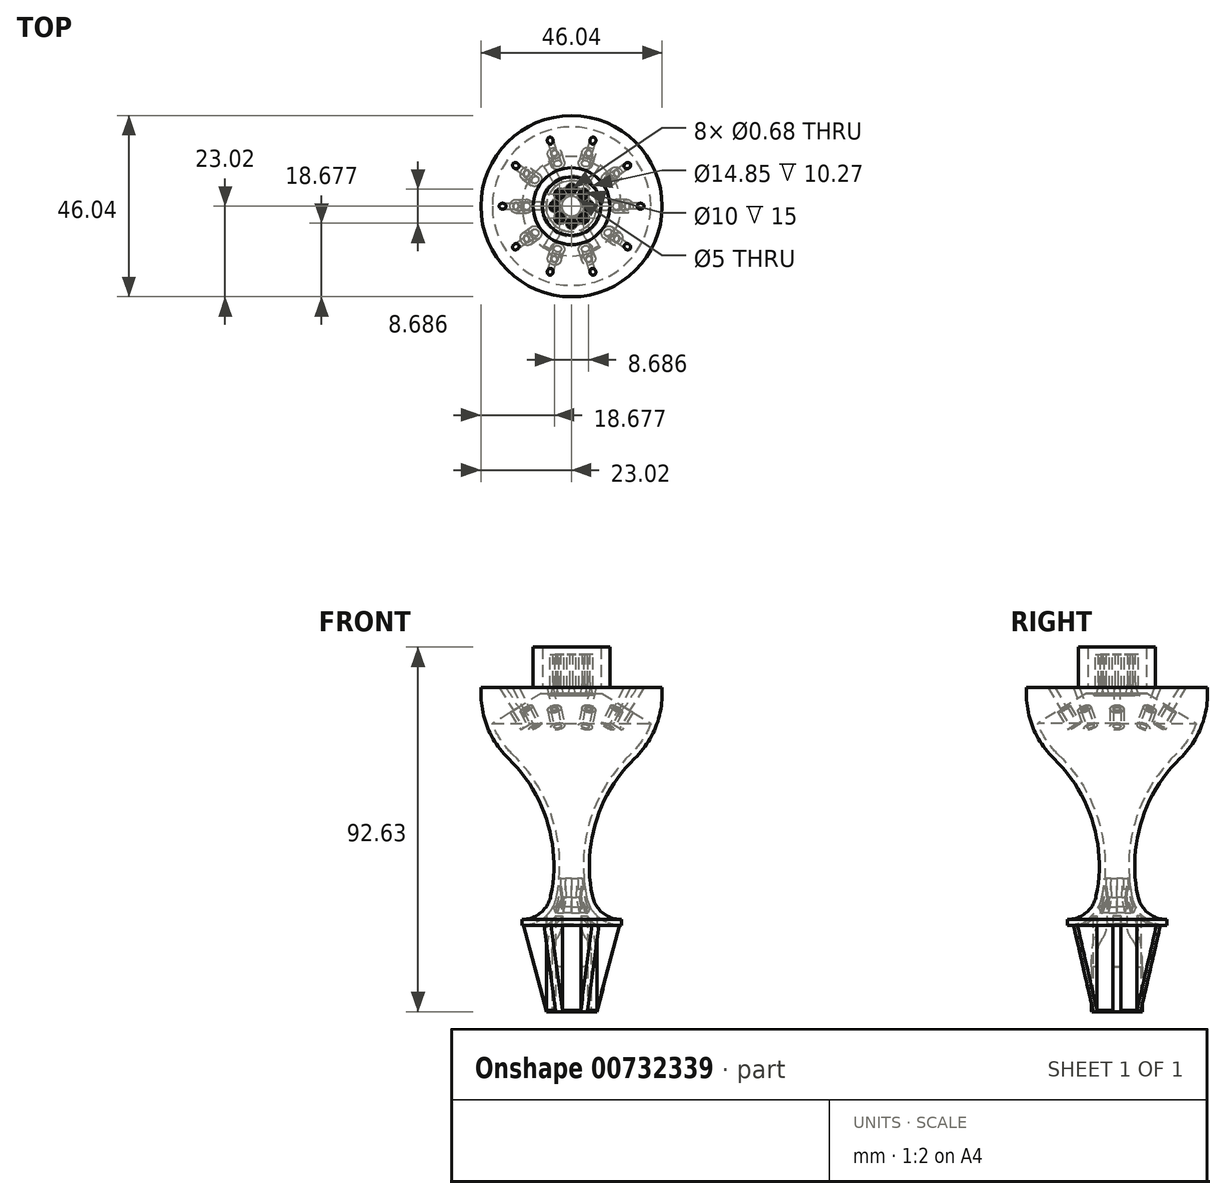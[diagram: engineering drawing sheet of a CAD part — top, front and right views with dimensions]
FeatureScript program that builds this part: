
annotation { "Feature Type Name" : "Feature", "Feature Type Description" : "" }
export const myFeature = defineFeature(function(context is Context, id is Id, definition is map)
    precondition{}
    {
        {
            var Q0;
            Q0=qCreatedBy(makeId("Front.planeOp"),FACE);
            var sketch = newSketch(context, id + "F0", { "sketchPlane" : qUnion([Q0])});
            skArc(sketch, "E0", {"start": v(16.02, 27.2) * mm, "mid": v(6.17, 11.12) * mm, "end": v(5.3, -7.72) * mm});
            skArc(sketch, "E1", {"start": v(5, -22.1) * mm, "mid": v(4.71, -20.36) * mm, "end": v(3.88, -18.8) * mm});
            skLineSegment(sketch, "E2", {"start": v(5, -22.1) * mm, "end": v(5, -37.1) * mm});
            skLineSegment(sketch, "E3", {"start": v(6.5, -25.66) * mm, "end": v(6.5, -37.1) * mm});
            skArc(sketch, "E4.trimOffspring", {"start": v(2.5, -14.83) * mm, "mid": v(2.87, -16.93) * mm, "end": v(3.88, -18.8) * mm});
            skLineSegment(sketch, "E5", {"start": v(6.5, -37.1) * mm, "end": v(5, -37.1) * mm});
            skArc(sketch, "E6.trimOffspring", {"start": v(29.62, -0.11) * mm, "mid": v(29.62, -0.06) * mm, "end": v(29.62, 0) * mm});
            skArc(sketch, "E7", {"start": v(6.5, -25.66) * mm, "mid": v(5.49, -16.67) * mm, "end": v(2.5, -8.12) * mm});
            skPoint(sketch, "E8.start.orphan", {"position": v(3, -9.22) * mm});
            skLineSegment(sketch, "E9", {"start": v(2.5, -14.83) * mm, "end": v(2.5, -8.12) * mm});
            skArc(sketch, "E10", {"start": v(14.97, 28.28) * mm, "mid": v(4.73, 11.56) * mm, "end": v(3.83, -8.02) * mm});
            skLineSegment(sketch, "E11", {"start": v(0, 43.76) * mm, "end": v(21.52, 43.76) * mm});
            skLineSegment(sketch, "E12", {"start": v(0, 43.76) * mm, "end": v(0, 45.26) * mm});
            skLineSegment(sketch, "E13", {"start": v(0, 45.26) * mm, "end": v(7.43, 45.26) * mm});
            skLineSegment(sketch, "E14", {"start": v(23.02, 45.26) * mm, "end": v(23.02, 43.76) * mm});
            skPoint(sketch, "E15", {"position": v(0, 0) * mm});
            skArc(sketch, "E16", {"start": v(14.97, 28.28) * mm, "mid": v(19.82, 35.35) * mm, "end": v(21.52, 43.76) * mm});
            skArc(sketch, "E17", {"start": v(16.02, 27.2) * mm, "mid": v(21.2, 34.77) * mm, "end": v(23.02, 43.76) * mm});
            skArc(sketch, "E18", {"start": v(3.83, -8.02) * mm, "mid": v(6.96, -13.17) * mm, "end": v(12.64, -15.19) * mm});
            skArc(sketch, "E19", {"start": v(5.3, -7.72) * mm, "mid": v(7.9, -12) * mm, "end": v(12.64, -13.69) * mm});
            skLineSegment(sketch, "E20", {"start": v(12.64, -13.69) * mm, "end": v(12.64, -15.19) * mm});
            skLineSegment(sketch, "E21.top", {"start": v(7.43, 55.53) * mm, "end": v(9.75, 55.53) * mm});
            skLineSegment(sketch, "E21.left", {"start": v(7.43, 45.26) * mm, "end": v(7.43, 55.53) * mm});
            skLineSegment(sketch, "E21.right", {"start": v(9.75, 45.26) * mm, "end": v(9.75, 55.53) * mm});
            skLineSegment(sketch, "E22.trimOffspring", {"start": v(9.75, 45.26) * mm, "end": v(23.02, 45.26) * mm});
            skPoint(sketch, "E23", {"position": v(3, 0) * mm});
            skSolve(sketch);
        }
        {
            var Q0;
            Q0 = qSketchRegion(id + "F0", true);
            var Q1;
            Q1=sQuery(id+"F0.wireOp",EDGE,"E12");
            revolve(context, id + "F1", {"surfaceOperationType" : NewSurfaceOperationType.NEW, "entities" : qUnion([Q0]), "axis" : qUnion([Q1]), "revolveType" : RevolveType.FULL});
        }
        {
            var Q0;
            Q0=qCreatedBy(makeId("Front.planeOp"),FACE);
            var sketch = newSketch(context, id + "F2", { "sketchPlane" : qUnion([Q0])});
            skLineSegment(sketch, "E24.bottom", {"start": v(4.34, 45.26) * mm, "end": v(4.85, 45.26) * mm});
            skLineSegment(sketch, "E24.top", {"start": v(4.34, 43.76) * mm, "end": v(5.25, 43.76) * mm});
            skLineSegment(sketch, "E24.left", {"start": v(4.34, 45.26) * mm, "end": v(4.34, 43.76) * mm});
            skLineSegment(sketch, "E25", {"start": v(4.85, 45.26) * mm, "end": v(5.25, 43.76) * mm});
            skSolve(sketch);
        }
        {
            var Q0;
            Q0=makeQuery(id+"F2.imprint","IMPRINT",FACE,{"disambiguationData":[TD([[makeQuery(id+"F2.imprint","IMPRINT",EDGE,{"derivedFrom":sQuery(id+"F2.wireOp",EDGE,"E24.bottom")}),-1.0]])]});
            var Q1;
            Q1=sQuery(id+"F2.wireOp",EDGE,"E24.left");
            revolve(context, id + "F3", {"surfaceOperationType" : NewSurfaceOperationType.NEW, "entities" : qUnion([Q0]), "axis" : qUnion([Q1]), "revolveType" : RevolveType.FULL});
        }
        {
            var Q0;
            Q0=makeQuery(id+"F3.opRevolve","SWEPT_BODY",BODY,{"disambiguationData":[OSD([sQuery(id+"F2.wireOp",EDGE,"E24.bottom"),sQuery(id+"F2.wireOp",EDGE,"E24.top"),sQuery(id+"F2.wireOp",EDGE,"E24.left"),sQuery(id+"F2.wireOp",EDGE,"E24.right")])]});
            var Q1;
            Q1=makeQuery(id+"F1.opRevolve","SWEPT_FACE",FACE,{"disambiguationData":[OSD([sQuery(id+"F0.wireOp",EDGE,"E14")])]});
            circularPattern(context, id + "F4", {"entities" : qUnion([Q0]), "axis" : qUnion([Q1]), "angle" : 360 * degree, "instanceCount" : 8, "equalSpace" : true});
        }
        {
            var Q0;
            Q0=makeQuery(id+"F3.opRevolve","SWEPT_BODY",BODY,{"disambiguationData":[OSD([sQuery(id+"F2.wireOp",EDGE,"E24.bottom"),sQuery(id+"F2.wireOp",EDGE,"E24.top"),sQuery(id+"F2.wireOp",EDGE,"E24.left"),sQuery(id+"F2.wireOp",EDGE,"E24.right")])]});
            var Q1;
            Q1=makeQuery(id+"F4.opPattern","COPY",BODY,{"derivedFrom":makeQuery(id+"F3.opRevolve","SWEPT_BODY",BODY,{"disambiguationData":[OSD([sQuery(id+"F2.wireOp",EDGE,"E24.bottom"),sQuery(id+"F2.wireOp",EDGE,"E24.top"),sQuery(id+"F2.wireOp",EDGE,"E24.left"),sQuery(id+"F2.wireOp",EDGE,"E24.right")])]}),"instanceName":"7"});
            var Q2;
            Q2=makeQuery(id+"F4.opPattern","COPY",BODY,{"derivedFrom":makeQuery(id+"F3.opRevolve","SWEPT_BODY",BODY,{"disambiguationData":[OSD([sQuery(id+"F2.wireOp",EDGE,"E24.bottom"),sQuery(id+"F2.wireOp",EDGE,"E24.top"),sQuery(id+"F2.wireOp",EDGE,"E24.left"),sQuery(id+"F2.wireOp",EDGE,"E24.right")])]}),"instanceName":"6"});
            var Q3;
            Q3=makeQuery(id+"F4.opPattern","COPY",BODY,{"derivedFrom":makeQuery(id+"F3.opRevolve","SWEPT_BODY",BODY,{"disambiguationData":[OSD([sQuery(id+"F2.wireOp",EDGE,"E24.bottom"),sQuery(id+"F2.wireOp",EDGE,"E24.top"),sQuery(id+"F2.wireOp",EDGE,"E24.left"),sQuery(id+"F2.wireOp",EDGE,"E24.right")])]}),"instanceName":"5"});
            var Q4;
            Q4=makeQuery(id+"F4.opPattern","COPY",BODY,{"derivedFrom":makeQuery(id+"F3.opRevolve","SWEPT_BODY",BODY,{"disambiguationData":[OSD([sQuery(id+"F2.wireOp",EDGE,"E24.bottom"),sQuery(id+"F2.wireOp",EDGE,"E24.top"),sQuery(id+"F2.wireOp",EDGE,"E24.left"),sQuery(id+"F2.wireOp",EDGE,"E24.right")])]}),"instanceName":"4"});
            var Q5;
            Q5=makeQuery(id+"F4.opPattern","COPY",BODY,{"derivedFrom":makeQuery(id+"F3.opRevolve","SWEPT_BODY",BODY,{"disambiguationData":[OSD([sQuery(id+"F2.wireOp",EDGE,"E24.bottom"),sQuery(id+"F2.wireOp",EDGE,"E24.top"),sQuery(id+"F2.wireOp",EDGE,"E24.left"),sQuery(id+"F2.wireOp",EDGE,"E24.right")])]}),"instanceName":"3"});
            var Q6;
            Q6=makeQuery(id+"F4.opPattern","COPY",BODY,{"derivedFrom":makeQuery(id+"F3.opRevolve","SWEPT_BODY",BODY,{"disambiguationData":[OSD([sQuery(id+"F2.wireOp",EDGE,"E24.bottom"),sQuery(id+"F2.wireOp",EDGE,"E24.top"),sQuery(id+"F2.wireOp",EDGE,"E24.left"),sQuery(id+"F2.wireOp",EDGE,"E24.right")])]}),"instanceName":"2"});
            var Q7;
            Q7=makeQuery(id+"F4.opPattern","COPY",BODY,{"derivedFrom":makeQuery(id+"F3.opRevolve","SWEPT_BODY",BODY,{"disambiguationData":[OSD([sQuery(id+"F2.wireOp",EDGE,"E24.bottom"),sQuery(id+"F2.wireOp",EDGE,"E24.top"),sQuery(id+"F2.wireOp",EDGE,"E24.left"),sQuery(id+"F2.wireOp",EDGE,"E24.right")])]}),"instanceName":"1"});
            var Q8;
            Q8=makeQuery(id+"F1.opRevolve","SWEPT_BODY",BODY,{"disambiguationData":[OSD([sQuery(id+"F0.wireOp",EDGE,"E0"),sQuery(id+"F0.wireOp",EDGE,"E10"),sQuery(id+"F0.wireOp",EDGE,"E11"),sQuery(id+"F0.wireOp",EDGE,"E12"),sQuery(id+"F0.wireOp",EDGE,"E13"),sQuery(id+"F0.wireOp",EDGE,"E14"),sQuery(id+"F0.wireOp",EDGE,"E16"),sQuery(id+"F0.wireOp",EDGE,"E17"),sQuery(id+"F0.wireOp",EDGE,"E18"),sQuery(id+"F0.wireOp",EDGE,"E19"),sQuery(id+"F0.wireOp",EDGE,"E20"),sQuery(id+"F0.wireOp",EDGE,"E21.top"),sQuery(id+"F0.wireOp",EDGE,"E21.left"),sQuery(id+"F0.wireOp",EDGE,"E21.right"),sQuery(id+"F0.wireOp",EDGE,"E22.trimOffspring")])]});
            booleanBodies(context, id + "F5", {"operationType" : BooleanOperationType.SUBTRACTION, "tools" : qUnion([Q0, Q1, Q2, Q3, Q4, Q5, Q6, Q7]), "targets" : qUnion([Q8])});
        }
        {
            var Q0;
            Q0=qCreatedBy(makeId("Top.planeOp"),FACE);
            var sketch = newSketch(context, id + "F6", { "sketchPlane" : qUnion([Q0])});
            skLineSegment(sketch, "E26.bottom", {"start": v(-74.62, 0) * mm, "end": v(74.62, 0) * mm});
            skLineSegment(sketch, "E26.top", {"start": v(-74.62, -35.92) * mm, "end": v(74.62, -35.92) * mm});
            skLineSegment(sketch, "E26.left", {"start": v(-74.62, 0) * mm, "end": v(-74.62, -35.92) * mm});
            skLineSegment(sketch, "E26.right", {"start": v(74.62, 0) * mm, "end": v(74.62, -35.92) * mm});
            skSolve(sketch);
        }
        {
            var Q0;
            Q0=qCreatedBy(makeId("Front.planeOp"),FACE);
            var sketch = newSketch(context, id + "F7", { "sketchPlane" : qUnion([Q0])});
            skLineSegment(sketch, "E27", {"start": v(17.45, 43.4) * mm, "end": v(12.2, 34.89) * mm});
            skLineSegment(sketch, "E28", {"start": v(12.2, 34.89) * mm, "end": v(12.87, 34.47) * mm});
            skLineSegment(sketch, "E29", {"start": v(12.87, 34.47) * mm, "end": v(18.13, 42.97) * mm});
            skLineSegment(sketch, "E30", {"start": v(18.13, 42.97) * mm, "end": v(17.45, 43.4) * mm});
            skSolve(sketch);
        }
        {
            var Q0;
            Q0=qCreatedBy(makeId("Front.planeOp"),FACE);
            var sketch = newSketch(context, id + "F8", { "sketchPlane" : qUnion([Q0])});
            skLineSegment(sketch, "E31", {"start": v(7.75, 43.76) * mm, "end": v(21.84, 43.76) * mm});
            skLineSegment(sketch, "E32", {"start": v(21.84, 43.76) * mm, "end": v(21.36, 35.38) * mm});
            skLineSegment(sketch, "E33", {"start": v(21.36, 35.38) * mm, "end": v(7.75, 43.76) * mm});
            skSolve(sketch);
        }
        {
            var Q0;
            Q0=qCreatedBy(makeId("Front.planeOp"),FACE);
            var sketch = newSketch(context, id + "F9", { "sketchPlane" : qUnion([Q0])});
            skLineSegment(sketch, "E34", {"start": v(20.58, 48.74) * mm, "end": v(14.45, 38.9) * mm});
            skLineSegment(sketch, "E35", {"start": v(14.45, 38.9) * mm, "end": v(13.8, 39.29) * mm});
            skLineSegment(sketch, "E36", {"start": v(13.8, 39.29) * mm, "end": v(19.94, 49.14) * mm});
            skLineSegment(sketch, "E37", {"start": v(20.58, 48.74) * mm, "end": v(19.94, 49.14) * mm});
            skSolve(sketch);
        }
        {
            var Q0;
            Q0=makeQuery(id+"F8.imprint","IMPRINT",FACE,{"disambiguationData":[TD([[makeQuery(id+"F8.imprint","IMPRINT",EDGE,{"derivedFrom":sQuery(id+"F8.wireOp",EDGE,"E31")}),-1.0]])]});
            var Q1;
            Q1=makeQuery(id+"F1.opRevolve","SWEPT_FACE",FACE,{"disambiguationData":[OSD([sQuery(id+"F0.wireOp",EDGE,"E14")])]});
            revolve(context, id + "F10", {"operationType" : NewBodyOperationType.ADD, "surfaceOperationType" : NewSurfaceOperationType.NEW, "entities" : qUnion([Q0]), "axis" : qUnion([Q1]), "revolveType" : RevolveType.FULL});
        }
        {
            var Q0;
            Q0=makeQuery(id+"F9.imprint","IMPRINT",FACE,{"disambiguationData":[TD([[makeQuery(id+"F9.imprint","IMPRINT",EDGE,{"derivedFrom":sQuery(id+"F9.wireOp",EDGE,"E34")}),-1.0]])]});
            var Q1;
            Q1=sQuery(id+"F9.wireOp",EDGE,"E36");
            revolve(context, id + "F11", {"surfaceOperationType" : NewSurfaceOperationType.NEW, "entities" : qUnion([Q0]), "axis" : qUnion([Q1]), "revolveType" : RevolveType.FULL});
        }
        {
            var Q0;
            Q0=makeQuery(id+"F11.opRevolve","SWEPT_BODY",BODY,{"disambiguationData":[OSD([sQuery(id+"F9.wireOp",EDGE,"E34"),sQuery(id+"F9.wireOp",EDGE,"E35"),sQuery(id+"F9.wireOp",EDGE,"E36"),sQuery(id+"F9.wireOp",EDGE,"E37")])]});
            var Q1;
            Q1=makeQuery(id+"F1.opRevolve","SWEPT_FACE",FACE,{"disambiguationData":[OSD([sQuery(id+"F0.wireOp",EDGE,"E14")])]});
            circularPattern(context, id + "F12", {"operationType" : NewBodyOperationType.REMOVE, "entities" : qUnion([Q0]), "axis" : qUnion([Q1]), "angle" : 360 * degree, "instanceCount" : 10, "equalSpace" : true});
        }
        {
            var Q0;
            Q0=makeQuery(id+"F7.imprint","IMPRINT",FACE,{"disambiguationData":[TD([[makeQuery(id+"F7.imprint","IMPRINT",EDGE,{"derivedFrom":sQuery(id+"F7.wireOp",EDGE,"E27")}),1.0]])]});
            var Q1;
            Q1=makeQuery(id+"F12.boolean.opBoolean","COPY",FACE,{"derivedFrom":makeQuery(id+"F11.opRevolve","SWEPT_FACE",FACE,{"disambiguationData":[OSD([sQuery(id+"F9.wireOp",EDGE,"E34")])]})});
            revolve(context, id + "F13", {"surfaceOperationType" : NewSurfaceOperationType.NEW, "entities" : qUnion([Q0]), "axis" : qUnion([Q1]), "revolveType" : RevolveType.FULL});
        }
        {
            var Q0;
            Q0=makeQuery(id+"F13.opRevolve","SWEPT_BODY",BODY,{"disambiguationData":[OSD([sQuery(id+"F7.wireOp",EDGE,"E27"),sQuery(id+"F7.wireOp",EDGE,"E28"),sQuery(id+"F7.wireOp",EDGE,"E29"),sQuery(id+"F7.wireOp",EDGE,"E30")])]});
            var Q1;
            Q1=makeQuery(id+"F1.opRevolve","SWEPT_FACE",FACE,{"disambiguationData":[OSD([sQuery(id+"F0.wireOp",EDGE,"E14")])]});
            circularPattern(context, id + "F14", {"operationType" : NewBodyOperationType.ADD, "entities" : qUnion([Q0]), "axis" : qUnion([Q1]), "angle" : 360 * degree, "instanceCount" : 10, "equalSpace" : true});
        }
        {
            var Q0;
            Q0=qCreatedBy(makeId("Front.planeOp"),FACE);
            var sketch = newSketch(context, id + "F15", { "sketchPlane" : qUnion([Q0])});
            skArc(sketch, "E38", {"start": v(5.27, 43.77) * mm, "mid": v(5.5, 43.44) * mm, "end": v(5.82, 43.2) * mm});
            skLineSegment(sketch, "E39", {"start": v(5.82, 43.77) * mm, "end": v(5.82, 43.2) * mm});
            skLineSegment(sketch, "E40", {"start": v(5.82, 43.77) * mm, "end": v(5.27, 43.77) * mm});
            skSolve(sketch);
        }
        {
            var Q0;
            Q0=makeQuery(id+"F15.imprint","IMPRINT",FACE,{"disambiguationData":[TD([[makeQuery(id+"F15.imprint","IMPRINT",EDGE,{"derivedFrom":sQuery(id+"F15.wireOp",EDGE,"E38")}),1.0]])]});
            var Q1;
            Q1=sQuery(id+"F2.wireOp",EDGE,"E24.left");
            revolve(context, id + "F16", {"surfaceOperationType" : NewSurfaceOperationType.NEW, "entities" : qUnion([Q0]), "axis" : qUnion([Q1]), "revolveType" : RevolveType.FULL});
        }
        {
            var Q0;
            Q0=makeQuery(id+"F16.opRevolve","SWEPT_BODY",BODY,{"disambiguationData":[OSD([sQuery(id+"F15.wireOp",EDGE,"E38"),sQuery(id+"F15.wireOp",EDGE,"E39"),sQuery(id+"F15.wireOp",EDGE,"E40")])]});
            var Q1;
            Q1=makeQuery(id+"F1.opRevolve","SWEPT_FACE",FACE,{"disambiguationData":[OSD([sQuery(id+"F0.wireOp",EDGE,"E14")])]});
            circularPattern(context, id + "F17", {"operationType" : NewBodyOperationType.ADD, "entities" : qUnion([Q0]), "axis" : qUnion([Q1]), "angle" : 360 * degree, "instanceCount" : 8, "equalSpace" : true});
        }
        {
            var Q0;
            Q0=qCreatedBy(makeId("Front.planeOp"),FACE);
            var sketch = newSketch(context, id + "F18", { "sketchPlane" : qUnion([Q0])});
            skArc(sketch, "E41", {"start": v(4.68, 46.5) * mm, "mid": v(4.73, 45.87) * mm, "end": v(4.85, 45.26) * mm});
            skLineSegment(sketch, "E42", {"start": v(5.48, 46.5) * mm, "end": v(5.48, 45.26) * mm});
            skLineSegment(sketch, "E43", {"start": v(5.48, 45.26) * mm, "end": v(4.85, 45.26) * mm});
            skLineSegment(sketch, "E44.top", {"start": v(4.68, 53.6) * mm, "end": v(5.48, 53.6) * mm});
            skLineSegment(sketch, "E44.left", {"start": v(4.68, 46.5) * mm, "end": v(4.68, 53.6) * mm});
            skLineSegment(sketch, "E44.right", {"start": v(5.48, 46.5) * mm, "end": v(5.48, 53.6) * mm});
            skSolve(sketch);
        }
        {
            var Q0;
            Q0=makeQuery(id+"F18.imprint","IMPRINT",FACE,{"disambiguationData":[TD([[makeQuery(id+"F18.imprint","IMPRINT",EDGE,{"derivedFrom":sQuery(id+"F18.wireOp",EDGE,"E41")}),1.0]])]});
            var Q1;
            Q1=sQuery(id+"F2.wireOp",EDGE,"E24.left");
            revolve(context, id + "F19", {"surfaceOperationType" : NewSurfaceOperationType.NEW, "entities" : qUnion([Q0]), "axis" : qUnion([Q1]), "revolveType" : RevolveType.FULL});
        }
        {
            var Q0;
            Q0=makeQuery(id+"F19.opRevolve","SWEPT_BODY",BODY,{"disambiguationData":[OSD([sQuery(id+"F18.wireOp",EDGE,"E41"),sQuery(id+"F18.wireOp",EDGE,"qMOBOxUs-DtZF-wELl-8FNL-C7Aba4HxzTed"),sQuery(id+"F18.wireOp",EDGE,"E42"),sQuery(id+"F18.wireOp",EDGE,"E43")])]});
            var Q1;
            Q1=makeQuery(id+"F1.opRevolve","SWEPT_FACE",FACE,{"disambiguationData":[OSD([sQuery(id+"F0.wireOp",EDGE,"E14")])]});
            circularPattern(context, id + "F20", {"entities" : qUnion([Q0]), "axis" : qUnion([Q1]), "angle" : 360 * degree, "instanceCount" : 4, "equalSpace" : true});
        }
        {
            var Q0;
            Q0=makeQuery(id+"F19.opRevolve","SWEPT_BODY",BODY,{"disambiguationData":[OSD([sQuery(id+"F18.wireOp",EDGE,"E41"),sQuery(id+"F18.wireOp",EDGE,"qMOBOxUs-DtZF-wELl-8FNL-C7Aba4HxzTed"),sQuery(id+"F18.wireOp",EDGE,"E42"),sQuery(id+"F18.wireOp",EDGE,"E43")])]});
            var Q1;
            Q1=makeQuery(id+"F1.opRevolve","SWEPT_FACE",FACE,{"disambiguationData":[OSD([sQuery(id+"F0.wireOp",EDGE,"E14")])]});
            circularPattern(context, id + "F21", {"operationType" : NewBodyOperationType.ADD, "entities" : qUnion([Q0]), "axis" : qUnion([Q1]), "angle" : 360 * degree, "instanceCount" : 8, "equalSpace" : true});
        }
        {
            var Q0;
            Q0=makeQuery(id+"F1.opRevolve","SWEPT_FACE",FACE,{"disambiguationData":[OSD([sQuery(id+"F0.wireOp",EDGE,"E5")])]});
            var sketch = newSketch(context, id + "F22", { "sketchPlane" : qUnion([Q0])});
            skArc(sketch, "E45", {"start": v(6.42, -1) * mm, "mid": v(6.5, 0) * mm, "end": v(6.42, 1) * mm});
            skLineSegment(sketch, "E46", {"start": v(6.42, 1) * mm, "end": v(12.2, 1) * mm});
            skLineSegment(sketch, "E47", {"start": v(12.2, 1) * mm, "end": v(12.2, 0) * mm});
            skLineSegment(sketch, "E48.MirrorCS", {"start": v(12.2, -1) * mm, "end": v(12.2, 0) * mm});
            skLineSegment(sketch, "E49", {"start": v(12.2, -1) * mm, "end": v(6.42, -1) * mm});
            skPoint(sketch, "E50.start.orphan", {"position": v(10.97, 0) * mm});
            skSolve(sketch);
        }
        {
            var Q0;
            Q0=makeQuery(id+"F22.imprint","IMPRINT",FACE,{"disambiguationData":[TD([[makeQuery(id+"F22.imprint","IMPRINT",EDGE,{"derivedFrom":sQuery(id+"F22.wireOp",EDGE,"E45")}),-1.0]])]});
            extrude(context, id + "F23", {"entities" : qUnion([Q0]), "endBound" : BoundingType.UP_TO_NEXT, "oppositeDirection" : true, "depth" : 25 * mm, "offsetDistance" : 25 * mm});
        }
        {
            var Q0;
            Q0=makeQuery(id+"F23.opExtrude","SWEPT_BODY",BODY,{"disambiguationData":[OSD([sQuery(id+"F22.wireOp",EDGE,"E45"),sQuery(id+"F22.wireOp",EDGE,"E46"),sQuery(id+"F22.wireOp",EDGE,"E47"),sQuery(id+"F22.wireOp",EDGE,"E48.MirrorCS"),sQuery(id+"F22.wireOp",EDGE,"E49")])]});
            var Q1;
            Q1=makeQuery(id+"F1.opRevolve","SWEPT_FACE",FACE,{"disambiguationData":[OSD([sQuery(id+"F0.wireOp",EDGE,"E2")])]});
            circularPattern(context, id + "F24", {"operationType" : NewBodyOperationType.ADD, "entities" : qUnion([Q0]), "axis" : qUnion([Q1]), "angle" : 360 * degree, "instanceCount" : 6, "equalSpace" : true});
        }
        {
            var Q0;
            Q0=qCreatedBy(makeId("Front.planeOp"),FACE);
            var sketch = newSketch(context, id + "F25", { "sketchPlane" : qUnion([Q0])});
            skLineSegment(sketch, "E51", {"start": v(6.42, -37.1) * mm, "end": v(12.2, -15.19) * mm});
            skLineSegment(sketch, "E52", {"start": v(12.2, -15.19) * mm, "end": v(15.57, -15.19) * mm});
            skLineSegment(sketch, "E53", {"start": v(15.57, -15.19) * mm, "end": v(15.57, -37.1) * mm});
            skLineSegment(sketch, "E54", {"start": v(6.42, -37.1) * mm, "end": v(15.57, -37.1) * mm});
            skSolve(sketch);
        }
        {
            var Q0;
            Q0=makeQuery(id+"F25.imprint","IMPRINT",FACE,{"disambiguationData":[TD([[makeQuery(id+"F25.imprint","IMPRINT",EDGE,{"derivedFrom":sQuery(id+"F25.wireOp",EDGE,"E51")}),-1.0]])]});
            var Q1;
            Q1=makeQuery(id+"F1.opRevolve","SWEPT_FACE",FACE,{"disambiguationData":[OSD([sQuery(id+"F0.wireOp",EDGE,"E2")])]});
            revolve(context, id + "F26", {"operationType" : NewBodyOperationType.REMOVE, "surfaceOperationType" : NewSurfaceOperationType.NEW, "entities" : qUnion([Q0]), "axis" : qUnion([Q1]), "revolveType" : RevolveType.FULL, "oppositeDirection" : true});
        }
        {
            var Q0;
            Q0=qCreatedBy(makeId("Front.planeOp"),FACE);
            var sketch = newSketch(context, id + "F27", { "sketchPlane" : qUnion([Q0])});
            skLineSegment(sketch, "E55", {"start": v(2.5, -8.12) * mm, "end": v(3.13, -3.2) * mm});
            skLineSegment(sketch, "E56", {"start": v(3.13, -3.2) * mm, "end": v(4.75, -10.52) * mm});
            skLineSegment(sketch, "E57", {"start": v(4.75, -10.52) * mm, "end": v(4.12, -12) * mm});
            skLineSegment(sketch, "E58", {"start": v(4.12, -12) * mm, "end": v(2.5, -12) * mm});
            skLineSegment(sketch, "E59", {"start": v(2.5, -12) * mm, "end": v(2.5, -8.12) * mm});
            skSolve(sketch);
        }
        {
            var Q0;
            Q0 = qSketchRegion(id + "F27", true);
            var Q1;
            Q1=makeQuery(id+"F1.opRevolve","SWEPT_FACE",FACE,{"disambiguationData":[OSD([sQuery(id+"F0.wireOp",EDGE,"E20")])]});
            revolve(context, id + "F28", {"surfaceOperationType" : NewSurfaceOperationType.NEW, "entities" : qUnion([Q0]), "axis" : qUnion([Q1]), "revolveType" : RevolveType.ONE_DIRECTION, "angle" : 30 * degree});
        }
        {
            var Q0;
            Q0=makeQuery(id+"F28.opRevolve","SWEPT_BODY",BODY,{"disambiguationData":[OSD([sQuery(id+"F27.wireOp",EDGE,"E55"),sQuery(id+"F27.wireOp",EDGE,"E56"),sQuery(id+"F27.wireOp",EDGE,"E57"),sQuery(id+"F27.wireOp",EDGE,"E58"),sQuery(id+"F27.wireOp",EDGE,"E59")])]});
            var Q1;
            Q1=makeQuery(id+"F1.opRevolve","SWEPT_FACE",FACE,{"disambiguationData":[OSD([sQuery(id+"F0.wireOp",EDGE,"E20")])]});
            circularPattern(context, id + "F29", {"operationType" : NewBodyOperationType.ADD, "entities" : qUnion([Q0]), "axis" : qUnion([Q1]), "angle" : 360 * degree, "instanceCount" : 6, "equalSpace" : true});
        }
    });
